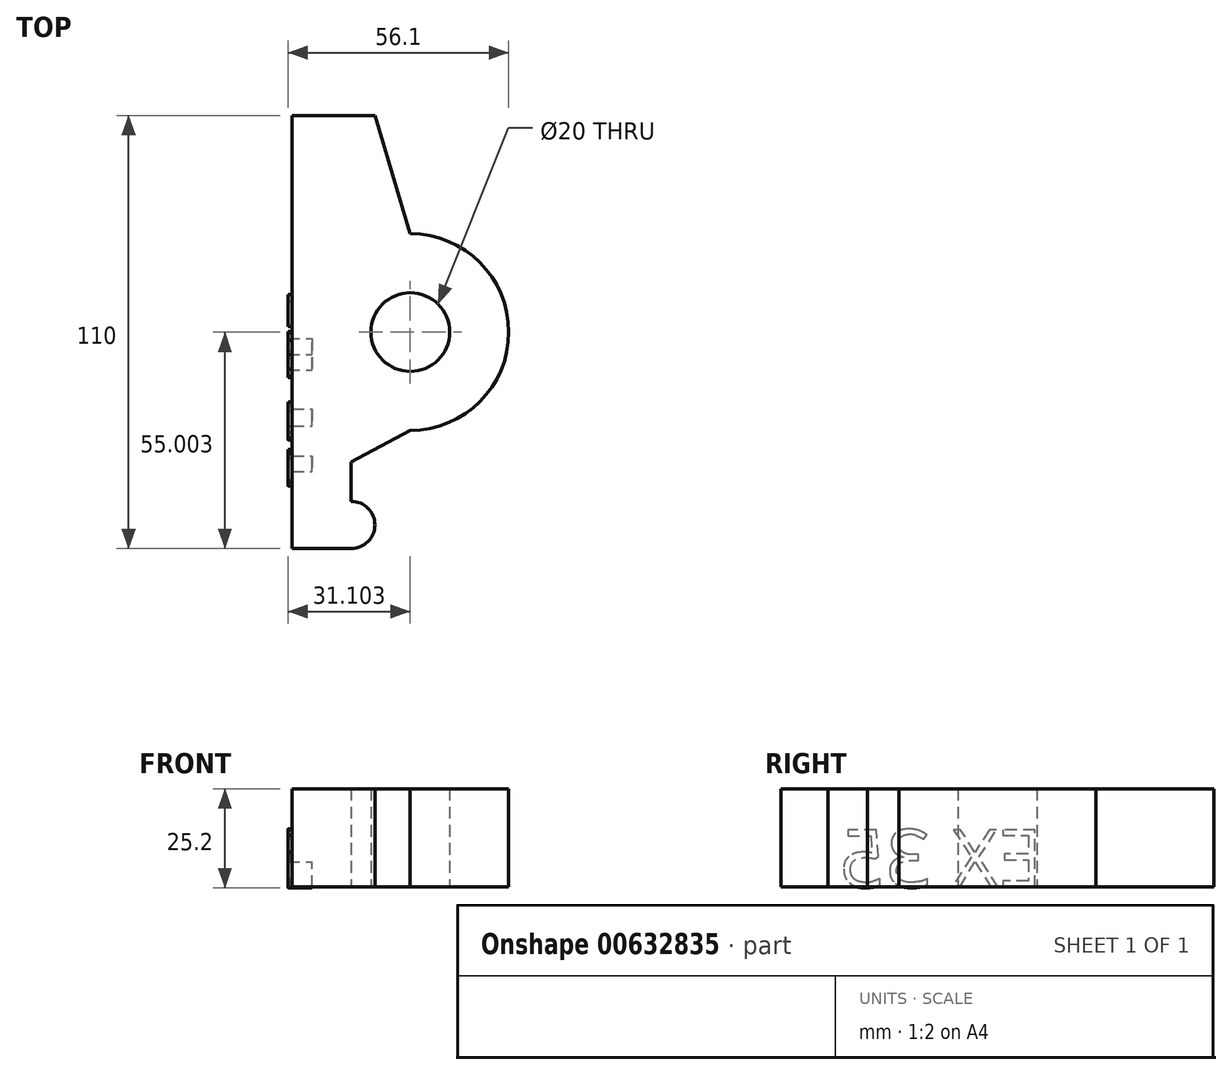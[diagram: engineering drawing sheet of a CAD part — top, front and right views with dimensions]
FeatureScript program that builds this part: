
annotation { "Feature Type Name" : "Feature", "Feature Type Description" : "" }
export const myFeature = defineFeature(function(context is Context, id is Id, definition is map)
    precondition{}
    {
        {
            var Q0;
            Q0=qCreatedBy(makeId("Top.planeOp"),FACE);
            var sketch = newSketch(context, id + "F0", { "sketchPlane" : qUnion([Q0])});
            skLineSegment(sketch, "E0", {"start": v(-14.69, 43.44) * mm, "end": v(1.31, 43.44) * mm});
            skLineSegment(sketch, "E1", {"start": v(1.31, 43.44) * mm, "end": v(10.31, 13.44) * mm});
            skLineSegment(sketch, "E2", {"start": v(-14.69, 43.44) * mm, "end": v(-14.69, -66.56) * mm});
            skLineSegment(sketch, "E3", {"start": v(-14.69, -66.56) * mm, "end": v(-4.69, -66.56) * mm});
            skArc(sketch, "E4", {"start": v(-4.69, -66.56) * mm, "mid": v(1.31, -60.56) * mm, "end": v(-4.69, -54.56) * mm});
            skLineSegment(sketch, "E5", {"start": v(-4.69, -54.56) * mm, "end": v(-4.69, -44.56) * mm});
            skLineSegment(sketch, "E6", {"start": v(-4.69, -44.56) * mm, "end": v(10.31, -36.56) * mm});
            skCircle(sketch, "E7", {"center": v(10.31, -11.56) * mm, "radius": 20 * mm});
            skPoint(sketch, "E7.centerSnap0", {"position": v(-14.69, -11.56) * mm});
            skCircle(sketch, "E8", {"center": v(10.31, -11.56) * mm, "radius": 25 * mm});
            skCircle(sketch, "E9", {"center": v(10.31, -11.56) * mm, "radius": 10 * mm});
            skSolve(sketch);
        }
        {
            var Q0;
            {var subQ0=sQuery(id+"F0.wireOp",EDGE,"E0");Q0=makeQuery(id+"F0.imprint","IMPRINT",FACE,{"disambiguationData":[TD([[makeQuery(id+"F0.imprint","IMPRINT",EDGE,{"derivedFrom":subQ0}),-1.0]])]});}
            var Q1;
            {var subQ0=sQuery(id+"F0.wireOp",EDGE,"E3");Q1=makeQuery(id+"F0.imprint","IMPRINT",FACE,{"disambiguationData":[TD([[makeQuery(id+"F0.imprint","IMPRINT",EDGE,{"derivedFrom":subQ0}),1.0]])]});}
            var Q2;
            Q2=makeQuery(id+"F0.imprint","IMPRINT",FACE,{"disambiguationData":[TD([[makeQuery(id+"F0.imprint","IMPRINT",EDGE,{"derivedFrom":sQuery(id+"F0.wireOp",EDGE,"E7")}),1.0]])]});
            var Q3;
            Q3=makeQuery(id+"F0.imprint","IMPRINT",FACE,{"disambiguationData":[TD([[makeQuery(id+"F0.imprint","IMPRINT",EDGE,{"derivedFrom":sQuery(id+"F0.wireOp",EDGE,"E7")}),-1.0]])]});
            extrude(context, id + "F1", {"entities" : qUnion([Q0, Q1, Q2, Q3]), "depth" : 25 * mm, "offsetDistance" : 25 * mm});
        }
        {
            var Q0;
            Q0=makeQuery(id+"F1.opExtrude","SWEPT_FACE",FACE,{"disambiguationData":[OSD([sQuery(id+"F0.wireOp",EDGE,"E2")])]});
            var sketch = newSketch(context, id + "F2", { "sketchPlane" : qUnion([Q0])});
            skText(sketch, "E10", { "text": "EX 35\n", "fontName": "OpenSans-Regular.ttf"});
            const initialGuessF2  = {"E10": [0, 0, 1, 0, 0.0147]};
            skSetInitialGuess(sketch, initialGuessF2);
            skSolve(sketch);
        }
        {
            var Q0;
            {var subQ8=sQuery(id+"F2.wireOp",EDGE,"E10.sketch_text.stroke-1");Q0=makeQuery(id+"F2.imprint","IMPRINT",FACE,{"disambiguationData":[TD([[makeQuery(id+"F2.imprint","IMPRINT",EDGE,{"derivedFrom":subQ8}),1.0]])]});}
            extrude(context, id + "F3", {"entities" : qUnion([Q0]), "operationType" : NewBodyOperationType.ADD, "depth" : 5 * mm, "offsetDistance" : 25 * mm});
        }
        {
            var Q0;
            Q0 = qSketchRegion(id + "F2", true);
            extrude(context, id + "F4", {"entities" : qUnion([Q0]), "operationType" : NewBodyOperationType.ADD, "depth" : 6.1 * mm, "offsetDistance" : 25 * mm});
        }
    });
